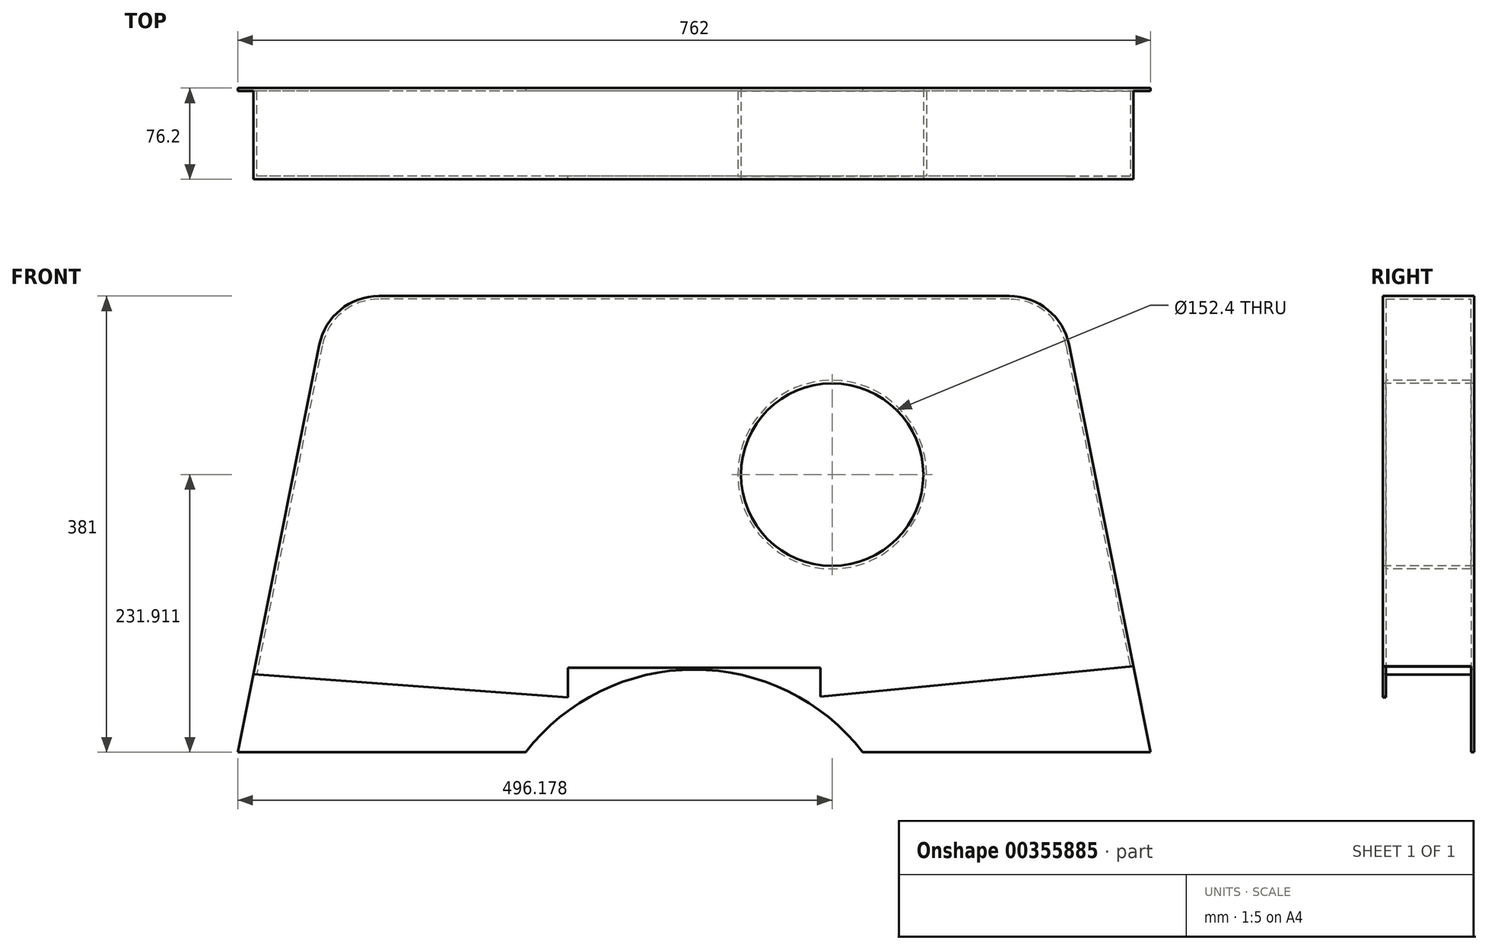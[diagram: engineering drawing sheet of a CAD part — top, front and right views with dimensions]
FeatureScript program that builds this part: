
annotation { "Feature Type Name" : "Feature", "Feature Type Description" : "" }
export const myFeature = defineFeature(function(context is Context, id is Id, definition is map)
    precondition{}
    {
        {
            var Q0;
            Q0=qCreatedBy(makeId("Top.planeOp"),FACE);
            var sketch = newSketch(context, id + "F0", { "sketchPlane" : qUnion([Q0])});
            skLineSegment(sketch, "E0.bottom", {"start": v(381, -38.1) * mm, "end": v(-381, -38.1) * mm});
            skLineSegment(sketch, "E0.top", {"start": v(381, 38.1) * mm, "end": v(-381, 38.1) * mm});
            skLineSegment(sketch, "E0.left", {"start": v(381, -38.1) * mm, "end": v(381, 38.1) * mm});
            skLineSegment(sketch, "E0.right", {"start": v(-381, -38.1) * mm, "end": v(-381, 38.1) * mm});
            skPoint(sketch, "E0.middle", {"position": v(0, 0) * mm});
            skSolve(sketch);
        }
        {
            var Q0;
            Q0=qSketchRegion(id+"F0",true);
            extrude(context, id + "F1", {"entities" : qUnion([Q0]), "depth" : 609.6 * mm});
        }
        {
            var Q0;
            Q0=makeQuery(id+"F1.opExtrude","SWEPT_FACE",FACE,{"disambiguationData":[OSD([sQuery(id+"F0.wireOp",EDGE,"E0.bottom")])]});
            var sketch = newSketch(context, id + "F2", { "sketchPlane" : qUnion([Q0])});
            skLineSegment(sketch, "E1", {"start": v(0, 381) * mm, "end": v(-304.8, 381) * mm});
            skLineSegment(sketch, "E2", {"start": v(-304.8, 381) * mm, "end": v(-381, 0) * mm});
            skLineSegment(sketch, "E3", {"start": v(0, 381) * mm, "end": v(304.8, 381) * mm});
            skLineSegment(sketch, "E4", {"start": v(304.8, 381) * mm, "end": v(381, 0) * mm});
            skPoint(sketch, "E5.center.orphan", {"position": v(0, 0) * mm});
            skSolve(sketch);
        }
        {
            var Q0;
            {var subQ1=sQuery(id+"F0.wireOp",EDGE,"E0.bottom");Q0=makeQuery(id+"F2.imprint","IMPRINT",FACE,{"disambiguationData":[TD([[makeQuery(id+"F2.imprint","IMPRINT",EDGE,{"derivedFrom":makeQuery(id+"F1.opExtrude","CAP_EDGE",EDGE,{"disambiguationData":[OSD([subQ1])],"isStart":false})}),1.0]])]});}
            extrude(context, id + "F3", {"entities" : qUnion([Q0]), "operationType" : NewBodyOperationType.REMOVE, "endBound" : BoundingType.THROUGH_ALL, "oppositeDirection" : true, "depth" : 25.4 * mm});
        }
        {
            var Q0;
            Q0=makeQuery(id+"F1.opExtrude","SWEPT_FACE",FACE,{"disambiguationData":[OSD([sQuery(id+"F0.wireOp",EDGE,"E0.bottom")])]});
            var sketch = newSketch(context, id + "F4", { "sketchPlane" : qUnion([Q0])});
            skCircle(sketch, "E6", {"center": v(115.18, 231.91) * mm, "radius": 76.2 * mm});
            skSolve(sketch);
        }
        {
            var Q0;
            Q0=makeQuery(id+"F4.imprint","IMPRINT",FACE,{"disambiguationData":[TD([[makeQuery(id+"F4.imprint","IMPRINT",EDGE,{"derivedFrom":sQuery(id+"F4.wireOp",EDGE,"E6")}),1.0]])]});
            extrude(context, id + "F5", {"entities" : qUnion([Q0]), "operationType" : NewBodyOperationType.REMOVE, "endBound" : BoundingType.THROUGH_ALL, "oppositeDirection" : true, "depth" : 25.4 * mm});
        }
        {
            var Q0;
            Q0=makeQuery(id+"F1.opExtrude","CAP_FACE",FACE,{"disambiguationData":[OSD([sQuery(id+"F0.wireOp",EDGE,"E0.bottom"),sQuery(id+"F0.wireOp",EDGE,"E0.top"),sQuery(id+"F0.wireOp",EDGE,"E0.left"),sQuery(id+"F0.wireOp",EDGE,"E0.right")])],"isStart":true});
            extrude(context, id + "F6", {"entities" : qUnion([Q0]), "operationType" : NewBodyOperationType.ADD, "depth" : 203.2 * mm});
        }
        {
            var Q0;
            {var subQ0=sQuery(id+"F0.wireOp",EDGE,"E0.top");Q0=makeQuery(id+"F6.boolean.opBoolean","MERGE",FACE,{"derivedFrom":[makeQuery(id+"F1.opExtrude","SWEPT_FACE",FACE,{"disambiguationData":[OSD([subQ0])]}),makeQuery(id+"F6.opExtrude","SWEPT_FACE",FACE,{"disambiguationData":[OSD([subQ0])]})]});}
            shell(context, id + "F7", {"entities" : qUnion([Q0]), "thickness" : 76.2 * mm});
        }
        {
            var Q0;
            {var subQ0=sQuery(id+"F0.wireOp",EDGE,"E0.top");Q0=makeQuery(id+"F6.boolean.opBoolean","MERGE",FACE,{"derivedFrom":[makeQuery(id+"F1.opExtrude","SWEPT_FACE",FACE,{"disambiguationData":[OSD([subQ0])]}),makeQuery(id+"F6.opExtrude","SWEPT_FACE",FACE,{"disambiguationData":[OSD([subQ0])]})]});}
            var sketch = newSketch(context, id + "F8", { "sketchPlane" : qUnion([Q0])});
            skLineSegment(sketch, "E7", {"start": v(381, 0) * mm, "end": v(-381, 0) * mm});
            skSolve(sketch);
        }
        {
            var Q0;
            {var subQ2=sQuery(id+"F0.wireOp",EDGE,"E0.top");Q0=makeQuery(id+"F8.imprint","IMPRINT",FACE,{"disambiguationData":[TD([[makeQuery(id+"F8.imprint","IMPRINT",EDGE,{"derivedFrom":makeQuery(id+"F7.opShell","OFFSET_EDGE",EDGE,{"disambiguationData":[OSD([subQ2])]})}),1.0]])]});}
            var Q1;
            {var subQ1=sQuery(id+"F0.wireOp",EDGE,"E0.top");Q1=makeQuery(id+"F8.imprint","IMPRINT",FACE,{"disambiguationData":[TD([[makeQuery(id+"F8.imprint","IMPRINT",EDGE,{"derivedFrom":makeQuery(id+"F6.opExtrude","CAP_EDGE",EDGE,{"disambiguationData":[OSD([subQ1])],"isStart":false})}),1.0]])]});}
            extrude(context, id + "F9", {"entities" : qUnion([Q0, Q1]), "operationType" : NewBodyOperationType.REMOVE, "endBound" : BoundingType.THROUGH_ALL, "oppositeDirection" : true, "depth" : 25.4 * mm});
        }
        {
            var Q0;
            Q0=qCreatedBy(makeId("Front.planeOp"),FACE);
            var sketch = newSketch(context, id + "F10", { "sketchPlane" : qUnion([Q0])});
            skCircle(sketch, "E8", {"center": v(0, -108.7) * mm, "radius": 177.8 * mm});
            skSolve(sketch);
        }
        {
            var Q0;
            Q0=qSketchRegion(id+"F10",true);
            extrude(context, id + "F11", {"entities" : qUnion([Q0]), "operationType" : NewBodyOperationType.REMOVE, "endBound" : BoundingType.SYMMETRIC, "oppositeDirection" : true, "depth" : 127 * mm});
        }
        {
            var Q0;
            {var subQ0=sQuery(id+"F0.wireOp",EDGE,"E0.bottom");Q0=makeQuery(id+"F6.boolean.opBoolean","MERGE",FACE,{"derivedFrom":[makeQuery(id+"F1.opExtrude","SWEPT_FACE",FACE,{"disambiguationData":[OSD([subQ0])]}),makeQuery(id+"F6.opExtrude","SWEPT_FACE",FACE,{"disambiguationData":[OSD([subQ0])]})]});}
            var sketch = newSketch(context, id + "F12", { "sketchPlane" : qUnion([Q0])});
            skLineSegment(sketch, "E9", {"start": v(-89.74, 44.8) * mm, "end": v(89.74, 44.8) * mm});
            skLineSegment(sketch, "E10", {"start": v(-89.74, 44.8) * mm, "end": v(-375.29, 65.72) * mm});
            skLineSegment(sketch, "E11", {"start": v(374.04, 72.49) * mm, "end": v(89.74, 44.8) * mm});
            skSolve(sketch);
        }
        {
            var Q0;
            {var subQ3=sQuery(id+"F0.wireOp",EDGE,"E0.bottom");var subQ4=makeQuery(id+"F6.boolean.opBoolean","MERGE",FACE,{"derivedFrom":[makeQuery(id+"F1.opExtrude","SWEPT_FACE",FACE,{"disambiguationData":[OSD([subQ3])]}),makeQuery(id+"F6.opExtrude","SWEPT_FACE",FACE,{"disambiguationData":[OSD([subQ3])]})]});var subQ7=makeQuery(id+"F11.boolean.opBoolean","SPLIT",EDGE,{"disambiguationData":[OD(1.0)],"derivedFrom":makeQuery(id+"F9.boolean.opBoolean","INTERSECT",EDGE,{"derivedFrom":[subQ4,makeQuery(id+"F9.opExtrude","SWEPT_FACE",FACE,{"disambiguationData":[OSD([sQuery(id+"F8.wireOp",EDGE,"E7")])]})]})});Q0=makeQuery(id+"F12.imprint","IMPRINT",FACE,{"disambiguationData":[TD([[makeQuery(id+"F12.imprint","IMPRINT",EDGE,{"derivedFrom":subQ7}),-1.0]])]});}
            var Q1;
            {var subQ3=sQuery(id+"F0.wireOp",EDGE,"E0.bottom");var subQ4=makeQuery(id+"F6.boolean.opBoolean","MERGE",FACE,{"derivedFrom":[makeQuery(id+"F1.opExtrude","SWEPT_FACE",FACE,{"disambiguationData":[OSD([subQ3])]}),makeQuery(id+"F6.opExtrude","SWEPT_FACE",FACE,{"disambiguationData":[OSD([subQ3])]})]});var subQ7=makeQuery(id+"F11.boolean.opBoolean","SPLIT",EDGE,{"disambiguationData":[OD(0.0)],"derivedFrom":makeQuery(id+"F9.boolean.opBoolean","INTERSECT",EDGE,{"derivedFrom":[subQ4,makeQuery(id+"F9.opExtrude","SWEPT_FACE",FACE,{"disambiguationData":[OSD([sQuery(id+"F8.wireOp",EDGE,"E7")])]})]})});Q1=makeQuery(id+"F12.imprint","IMPRINT",FACE,{"disambiguationData":[TD([[makeQuery(id+"F12.imprint","IMPRINT",EDGE,{"derivedFrom":subQ7}),-1.0]])]});}
            extrude(context, id + "F13", {"entities" : qUnion([Q0, Q1]), "operationType" : NewBodyOperationType.REMOVE, "oppositeDirection" : true, "depth" : 73.66 * mm});
        }
        {
            var Q0;
            Q0=makeQuery(id+"F3.boolean.opBoolean","COPY",EDGE,{"derivedFrom":makeQuery(id+"F3.opExtrude","SWEPT_EDGE",EDGE,{"disambiguationData":[OSD([sQuery(id+"F2.wireOp",EDGE,"E1"),sQuery(id+"F2.wireOp",EDGE,"E2")])]})});
            var Q1;
            Q1=makeQuery(id+"F3.boolean.opBoolean","COPY",EDGE,{"derivedFrom":makeQuery(id+"F3.opExtrude","SWEPT_EDGE",EDGE,{"disambiguationData":[OSD([sQuery(id+"F2.wireOp",EDGE,"E3"),sQuery(id+"F2.wireOp",EDGE,"E4")])]})});
            fillet(context, id + "F14", {"entities" : qUnion([Q0, Q1]), "radius" : 50.8 * mm, "tangentPropagation" : true, "allowEdgeOverflow" : false});
        }
        {
            var Q0;
            Q0=makeQuery(id+"F11.boolean.opBoolean","COPY",FACE,{"derivedFrom":makeQuery(id+"F11.opExtrude","SWEPT_FACE",FACE,{"disambiguationData":[OSD([sQuery(id+"F10.wireOp",EDGE,"E8")])]})});
            var Q1;
            Q1=makeQuery(id+"F13.boolean.opBoolean","COPY",FACE,{"derivedFrom":makeQuery(id+"F13.opExtrude","SWEPT_FACE",FACE,{"disambiguationData":[OSD([sQuery(id+"F12.wireOp",EDGE,"E10")])]})});
            var Q2;
            Q2=makeQuery(id+"F13.boolean.opBoolean","COPY",FACE,{"derivedFrom":makeQuery(id+"F13.opExtrude","SWEPT_FACE",FACE,{"disambiguationData":[OSD([sQuery(id+"F12.wireOp",EDGE,"E11")])]})});
            shell(context, id + "F15", {"entities" : qUnion([Q0, Q1, Q2]), "thickness" : 2.54 * mm});
        }
        {
            var Q0;
            {var subQ0=sQuery(id+"F0.wireOp",EDGE,"E0.bottom");Q0=makeQuery(id+"F6.boolean.opBoolean","MERGE",FACE,{"derivedFrom":[makeQuery(id+"F1.opExtrude","SWEPT_FACE",FACE,{"disambiguationData":[OSD([subQ0])]}),makeQuery(id+"F6.opExtrude","SWEPT_FACE",FACE,{"disambiguationData":[OSD([subQ0])]})]});}
            var sketch = newSketch(context, id + "F16", { "sketchPlane" : qUnion([Q0])});
            skLineSegment(sketch, "E12.bottom", {"start": v(105.5, 12.76) * mm, "end": v(-105.5, 12.76) * mm});
            skLineSegment(sketch, "E12.top", {"start": v(105.5, 70.56) * mm, "end": v(-105.5, 70.56) * mm});
            skLineSegment(sketch, "E12.left", {"start": v(105.5, 12.76) * mm, "end": v(105.5, 70.56) * mm});
            skLineSegment(sketch, "E12.right", {"start": v(-105.5, 12.76) * mm, "end": v(-105.5, 70.56) * mm});
            skPoint(sketch, "E12.middle", {"position": v(0, 41.66) * mm});
            skSolve(sketch);
        }
        {
            var Q0;
            Q0=qSketchRegion(id+"F16",true);
            extrude(context, id + "F17", {"entities" : qUnion([Q0]), "operationType" : NewBodyOperationType.REMOVE, "oppositeDirection" : true, "depth" : 25.4 * mm});
        }
    });
